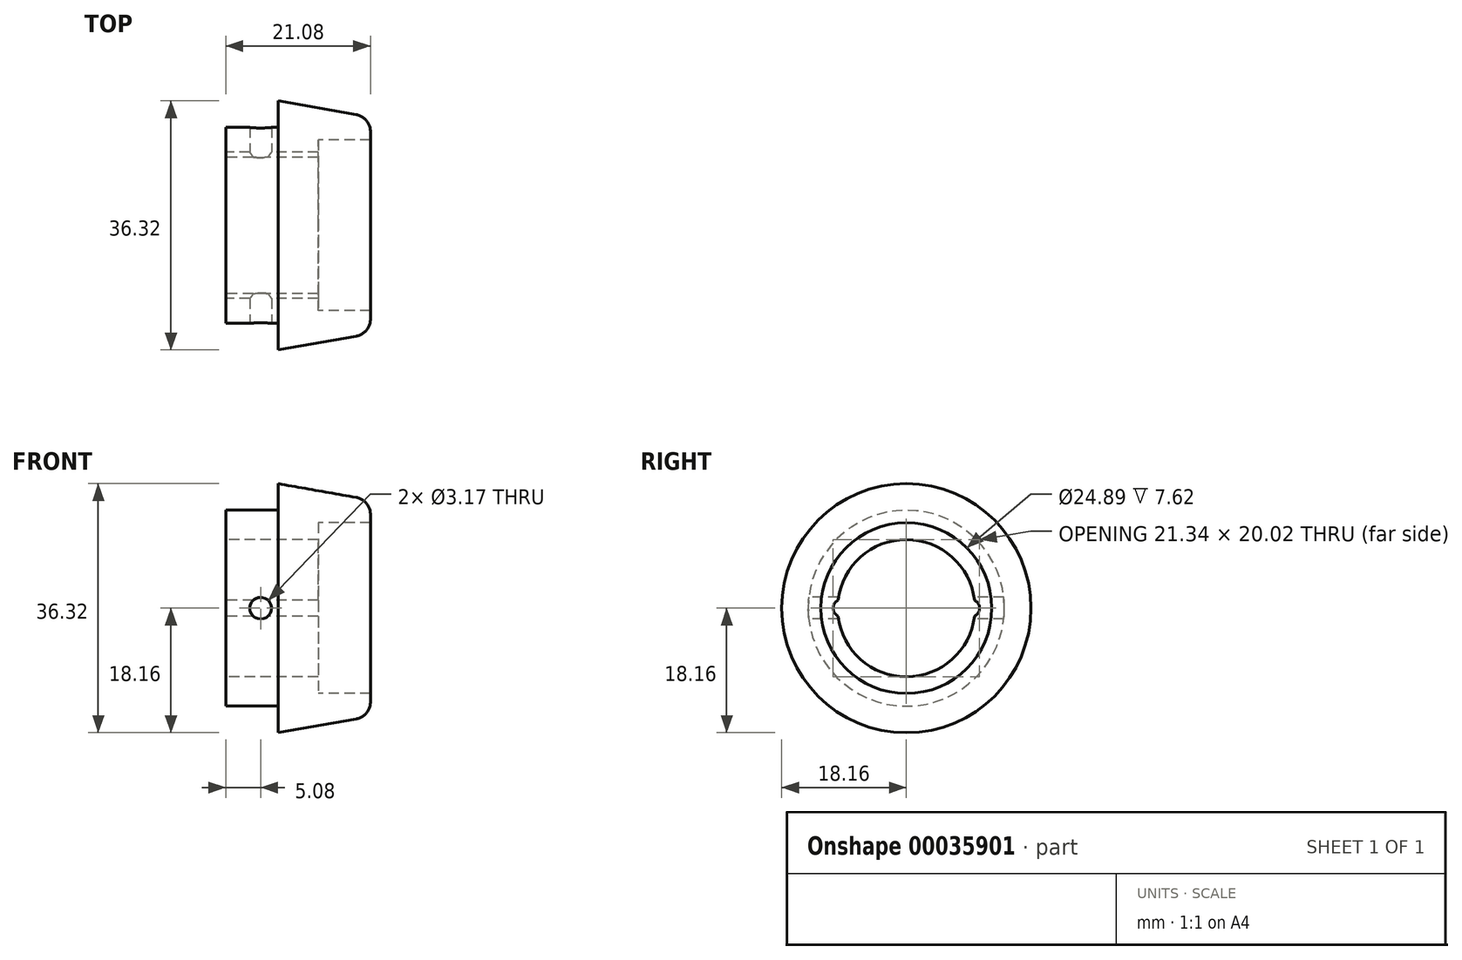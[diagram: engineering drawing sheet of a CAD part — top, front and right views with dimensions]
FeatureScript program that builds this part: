
annotation { "Feature Type Name" : "Feature", "Feature Type Description" : "" }
export const myFeature = defineFeature(function(context is Context, id is Id, definition is map)
    precondition{}
    {
        {
            var Q0;
            Q0=qCreatedBy(makeId("Front.planeOp"),FACE);
            var sketch = newSketch(context, id + "F0", { "sketchPlane" : qUnion([Q0])});
            skLineSegment(sketch, "E0", {"start": v(7.62, 14.29) * mm, "end": v(0, 14.29) * mm});
            skLineSegment(sketch, "E1", {"start": v(0, 14.29) * mm, "end": v(0, 10) * mm});
            skLineSegment(sketch, "E2", {"start": v(0, 10) * mm, "end": v(13.46, 10) * mm});
            skLineSegment(sketch, "E3", {"start": v(13.46, 10) * mm, "end": v(13.46, 12.45) * mm});
            skLineSegment(sketch, "E4", {"start": v(13.46, 12.45) * mm, "end": v(21.08, 12.45) * mm});
            skLineSegment(sketch, "E5", {"start": v(7.62, 18.16) * mm, "end": v(7.62, 14.29) * mm});
            skLineSegment(sketch, "E6", {"start": v(7.62, 18.16) * mm, "end": v(21.08, 15.79) * mm});
            skLineSegment(sketch, "E7", {"start": v(21.08, 15.79) * mm, "end": v(21.08, 12.45) * mm});
            skLineSegment(sketch, "E8", {"start": v(0, 0) * mm, "end": v(21.08, 0) * mm, "construction": true});
            skSolve(sketch);
        }
        {
            var Q0;
            Q0=makeQuery(id+"F0.imprint","IMPRINT",FACE,{"disambiguationData":[TD([[makeQuery(id+"F0.imprint","IMPRINT",EDGE,{"derivedFrom":sQuery(id+"F0.wireOp",EDGE,"E0")}),1.0]])]});
            var Q1;
            Q1=sQuery(id+"F0.wireOp",EDGE,"E8");
            revolve(context, id + "F1", {"entities" : qUnion([Q0]), "axis" : qUnion([Q1]), "revolveType" : RevolveType.FULL});
        }
        {
            var Q0;
            Q0=makeQuery(id+"F1.opRevolve","SWEPT_EDGE",EDGE,{"disambiguationData":[OSD([sQuery(id+"F0.wireOp",EDGE,"E6"),sQuery(id+"F0.wireOp",EDGE,"E7")])]});
            fillet(context, id + "F2", {"entities" : qUnion([Q0]), "radius" : 2.54 * mm, "tangentPropagation" : true, "allowEdgeOverflow" : false});
        }
        {
            var Q0;
            Q0=qCreatedBy(makeId("Right.planeOp"),FACE);
            var sketch = newSketch(context, id + "F3", { "sketchPlane" : qUnion([Q0])});
            skCircle(sketch, "E9.0", {"center": v(0, 0) * mm, "radius": 10 * mm});
            skLineSegment(sketch, "E10", {"start": v(-9.4, 0) * mm, "end": v(9.4, 0) * mm, "construction": true});
            skCircle(sketch, "E11", {"center": v(-9.4, 0) * mm, "radius": 1.27 * mm});
            skCircle(sketch, "E12", {"center": v(9.4, 0) * mm, "radius": 1.27 * mm});
            skSolve(sketch);
        }
        {
            var Q0;
            {var subQ0=sQuery(id+"F3.wireOp",EDGE,"E11");var subQ1=sQuery(id+"F3.wireOp",EDGE,"E9.0");var subQ3=makeQuery(id+"F3.imprint","INTERSECT",VERTEX,{"disambiguationData":[OD(0.0)],"derivedFrom":[subQ1,subQ0]});Q0=makeQuery(id+"F3.imprint","IMPRINT",FACE,{"disambiguationData":[TD([[makeQuery(id+"F3.imprint","IMPRINT",EDGE,{"disambiguationData":[TD([[subQ3,-1.0]])],"derivedFrom":subQ1}),-1.0]])]});}
            var Q1;
            {var subQ0=sQuery(id+"F3.wireOp",EDGE,"E12");var subQ1=sQuery(id+"F3.wireOp",EDGE,"E9.0");var subQ3=makeQuery(id+"F3.imprint","INTERSECT",VERTEX,{"disambiguationData":[OD(0.0)],"derivedFrom":[subQ1,subQ0]});Q1=makeQuery(id+"F3.imprint","IMPRINT",FACE,{"disambiguationData":[TD([[makeQuery(id+"F3.imprint","IMPRINT",EDGE,{"disambiguationData":[TD([[subQ3,1.0]])],"derivedFrom":subQ1}),-1.0]])]});}
            extrude(context, id + "F4", {"entities" : qUnion([Q0, Q1]), "operationType" : NewBodyOperationType.REMOVE, "endBound" : BoundingType.THROUGH_ALL, "depth" : 25.4 * mm});
        }
        {
            var Q0;
            Q0=qCreatedBy(makeId("Front.planeOp"),FACE);
            var sketch = newSketch(context, id + "F5", { "sketchPlane" : qUnion([Q0])});
            skCircle(sketch, "E13", {"center": v(5.08, 0) * mm, "radius": 1.59 * mm});
            skSolve(sketch);
        }
        {
            var Q0;
            Q0 = qSketchRegion(id + "F5", true);
            extrude(context, id + "F6", {"entities" : qUnion([Q0]), "operationType" : NewBodyOperationType.REMOVE, "endBound" : BoundingType.THROUGH_ALL, "oppositeDirection" : true, "depth" : 25.4 * mm, "hasSecondDirection" : true, "secondDirectionBound" : BoundingType.THROUGH_ALL, "secondDirectionOppositeDirection" : false, "secondDirectionDepth" : 25.4 * mm});
        }
    });
